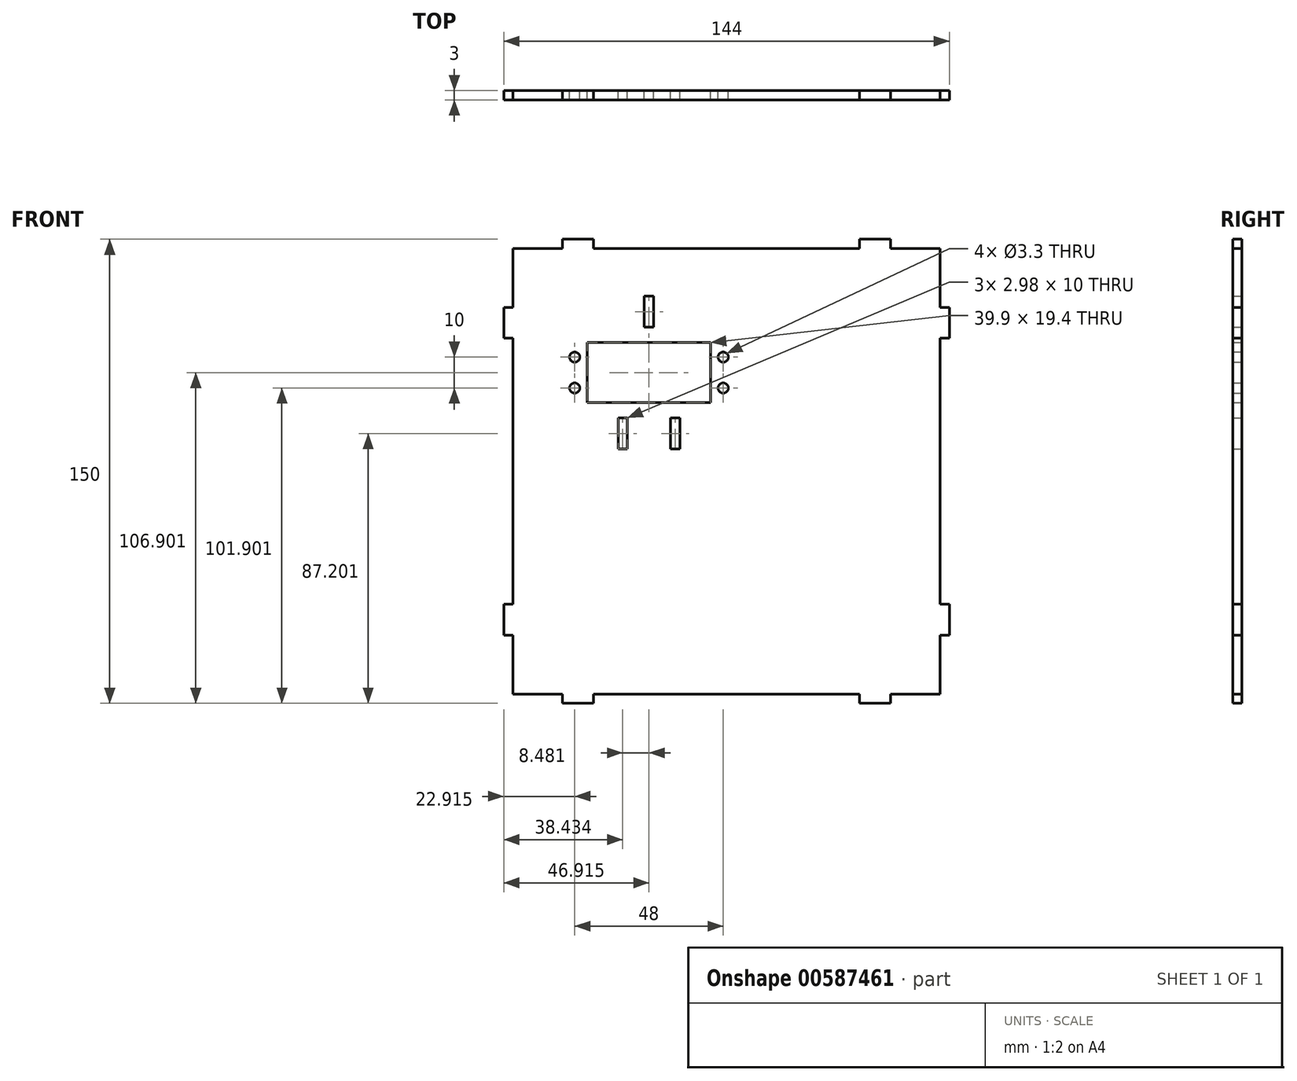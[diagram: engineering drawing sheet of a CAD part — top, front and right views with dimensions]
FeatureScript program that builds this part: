
annotation { "Feature Type Name" : "Feature", "Feature Type Description" : "" }
export const myFeature = defineFeature(function(context is Context, id is Id, definition is map)
    precondition{}
    {
        {
            var Q0;
            Q0=qCreatedBy(makeId("Front.planeOp"),FACE);
            var sketch = newSketch(context, id + "F0", { "sketchPlane" : qUnion([Q0])});
            skLineSegment(sketch, "E0", {"start": v(53, -75) * mm, "end": v(53, -72) * mm});
            skLineSegment(sketch, "E1", {"start": v(53, -72) * mm, "end": v(69, -72) * mm});
            skLineSegment(sketch, "E2", {"start": v(53, -75) * mm, "end": v(43, -75) * mm});
            skLineSegment(sketch, "E3", {"start": v(43, -75) * mm, "end": v(43, -72) * mm});
            skLineSegment(sketch, "E4", {"start": v(43, -72) * mm, "end": v(-43, -72) * mm});
            skLineSegment(sketch, "E5", {"start": v(-43, -72) * mm, "end": v(-43, -75) * mm});
            skLineSegment(sketch, "E6", {"start": v(-43, -75) * mm, "end": v(-53, -75) * mm});
            skLineSegment(sketch, "E7", {"start": v(-53, -75) * mm, "end": v(-53, -72) * mm});
            skLineSegment(sketch, "E8", {"start": v(-53, -72) * mm, "end": v(-69, -72) * mm});
            skLineSegment(sketch, "E9", {"start": v(0, 0) * mm, "end": v(0, -122.28) * mm, "construction": true});
            skPoint(sketch, "E9.endSnap0", {"position": v(0, -72) * mm});
            skLineSegment(sketch, "E10", {"start": v(-53, 75) * mm, "end": v(-53, 72) * mm});
            skLineSegment(sketch, "E11", {"start": v(-53, 72) * mm, "end": v(-69, 72) * mm});
            skLineSegment(sketch, "E12", {"start": v(-53, 75) * mm, "end": v(-43, 75) * mm});
            skLineSegment(sketch, "E13", {"start": v(-43, 75) * mm, "end": v(-43, 72) * mm});
            skLineSegment(sketch, "E14", {"start": v(-43, 72) * mm, "end": v(43, 72) * mm});
            skLineSegment(sketch, "E15", {"start": v(43, 72) * mm, "end": v(43, 75) * mm});
            skLineSegment(sketch, "E16", {"start": v(43, 75) * mm, "end": v(53, 75) * mm});
            skLineSegment(sketch, "E17", {"start": v(53, 75) * mm, "end": v(53, 72) * mm});
            skLineSegment(sketch, "E18", {"start": v(53, 72) * mm, "end": v(69, 72) * mm});
            skLineSegment(sketch, "E19", {"start": v(-69, -72) * mm, "end": v(-69, -53) * mm});
            skLineSegment(sketch, "E20", {"start": v(-69, -53) * mm, "end": v(-72, -53) * mm});
            skLineSegment(sketch, "E21", {"start": v(-72, -53) * mm, "end": v(-72, -43) * mm});
            skLineSegment(sketch, "E22", {"start": v(-72, -43) * mm, "end": v(-69, -43) * mm});
            skLineSegment(sketch, "E23", {"start": v(-69, -43) * mm, "end": v(-69, 43) * mm});
            skLineSegment(sketch, "E24", {"start": v(-69, 43) * mm, "end": v(-72, 43) * mm});
            skLineSegment(sketch, "E25", {"start": v(-72, 43) * mm, "end": v(-72, 53) * mm});
            skLineSegment(sketch, "E26", {"start": v(-72, 53) * mm, "end": v(-69, 53) * mm});
            skLineSegment(sketch, "E27", {"start": v(-69, 53) * mm, "end": v(-69, 72) * mm});
            skLineSegment(sketch, "E28", {"start": v(69, 72) * mm, "end": v(69, 53) * mm});
            skLineSegment(sketch, "E29", {"start": v(69, 53) * mm, "end": v(72, 53) * mm});
            skLineSegment(sketch, "E30", {"start": v(72, 53) * mm, "end": v(72, 43) * mm});
            skLineSegment(sketch, "E31", {"start": v(72, 43) * mm, "end": v(69, 43) * mm});
            skLineSegment(sketch, "E32", {"start": v(69, 43) * mm, "end": v(69, -43) * mm});
            skLineSegment(sketch, "E33", {"start": v(69, -43) * mm, "end": v(72, -43) * mm});
            skLineSegment(sketch, "E34", {"start": v(72, -43) * mm, "end": v(72, -53) * mm});
            skLineSegment(sketch, "E35", {"start": v(72, -53) * mm, "end": v(69, -53) * mm});
            skLineSegment(sketch, "E36", {"start": v(69, -53) * mm, "end": v(69, -72) * mm});
            skLineSegment(sketch, "E37.top", {"start": v(-45.04, 41.6) * mm, "end": v(-5.14, 41.6) * mm});
            skLineSegment(sketch, "E37.left", {"start": v(-45.04, 22.2) * mm, "end": v(-45.04, 41.6) * mm});
            skLineSegment(sketch, "E37.right", {"start": v(-5.14, 22.2) * mm, "end": v(-5.14, 41.6) * mm});
            skLineSegment(sketch, "E38", {"start": v(-45.04, 31.9) * mm, "end": v(-5.14, 31.9) * mm, "construction": true});
            skLineSegment(sketch, "E39", {"start": v(-25.09, 41.6) * mm, "end": v(-25.09, 22.2) * mm, "construction": true});
            skLineSegment(sketch, "E40.MirrorCS", {"start": v(-5.14, 22.2) * mm, "end": v(-45.04, 22.2) * mm});
            skCircle(sketch, "E41", {"center": v(-49.09, 36.9) * mm, "radius": 1.65 * mm});
            skCircle(sketch, "E42.0.1.0", {"center": v(-49.09, 26.9) * mm, "radius": 1.65 * mm});
            skLineSegment(sketch, "E42.direction1", {"start": v(-49.09, 36.9) * mm, "end": v(-24.09, 36.9) * mm, "construction": true});
            skLineSegment(sketch, "E42.direction2", {"start": v(-49.09, 36.9) * mm, "end": v(-49.09, 26.9) * mm, "construction": true});
            skCircle(sketch, "E43.MirrorC", {"center": v(-1.09, 36.9) * mm, "radius": 1.65 * mm});
            skCircle(sketch, "E44.MirrorC", {"center": v(-1.09, 26.9) * mm, "radius": 1.65 * mm});
            skLineSegment(sketch, "E45.MirrorCS", {"start": v(-1.09, 36.9) * mm, "end": v(-1.09, 26.9) * mm, "construction": true});
            skLineSegment(sketch, "E46.MirrorCS", {"start": v(-1.09, 36.9) * mm, "end": v(-26.09, 36.9) * mm, "construction": true});
            skLineSegment(sketch, "E47", {"start": v(-35.06, 22.2) * mm, "end": v(-35.06, 17.2) * mm, "construction": true});
            skLineSegment(sketch, "E48.bottom", {"start": v(-35.06, 17.2) * mm, "end": v(-32.08, 17.2) * mm});
            skLineSegment(sketch, "E48.top", {"start": v(-35.06, 7.2) * mm, "end": v(-32.08, 7.2) * mm});
            skLineSegment(sketch, "E48.left", {"start": v(-35.06, 17.2) * mm, "end": v(-35.06, 7.2) * mm});
            skLineSegment(sketch, "E48.right", {"start": v(-32.08, 17.2) * mm, "end": v(-32.08, 7.2) * mm});
            skLineSegment(sketch, "E49.MirrorCS", {"start": v(-15.11, 22.2) * mm, "end": v(-15.11, 17.2) * mm, "construction": true});
            skLineSegment(sketch, "E50.MirrorCS", {"start": v(-15.11, 7.2) * mm, "end": v(-18.1, 7.2) * mm});
            skLineSegment(sketch, "E51.MirrorCS", {"start": v(-15.11, 17.2) * mm, "end": v(-15.11, 7.2) * mm});
            skLineSegment(sketch, "E52.MirrorCS", {"start": v(-18.1, 17.2) * mm, "end": v(-18.1, 7.2) * mm});
            skLineSegment(sketch, "E53.MirrorCS", {"start": v(-15.11, 17.2) * mm, "end": v(-18.1, 17.2) * mm});
            skLineSegment(sketch, "E54", {"start": v(-25.09, 41.6) * mm, "end": v(-25.09, 46.6) * mm, "construction": true});
            skLineSegment(sketch, "E55.bottom", {"start": v(-26.58, 46.6) * mm, "end": v(-23.6, 46.6) * mm});
            skLineSegment(sketch, "E55.top", {"start": v(-26.58, 56.6) * mm, "end": v(-23.6, 56.6) * mm});
            skLineSegment(sketch, "E55.left", {"start": v(-26.58, 46.6) * mm, "end": v(-26.58, 56.6) * mm});
            skLineSegment(sketch, "E55.right", {"start": v(-23.6, 46.6) * mm, "end": v(-23.6, 56.6) * mm});
            skSolve(sketch);
        }
        {
            var Q0;
            Q0 = qSketchRegion(id + "F0", true);
            extrude(context, id + "F1", {"entities" : qUnion([Q0]), "depth" : 3 * mm, "offsetDistance" : 25 * mm});
        }
    });
